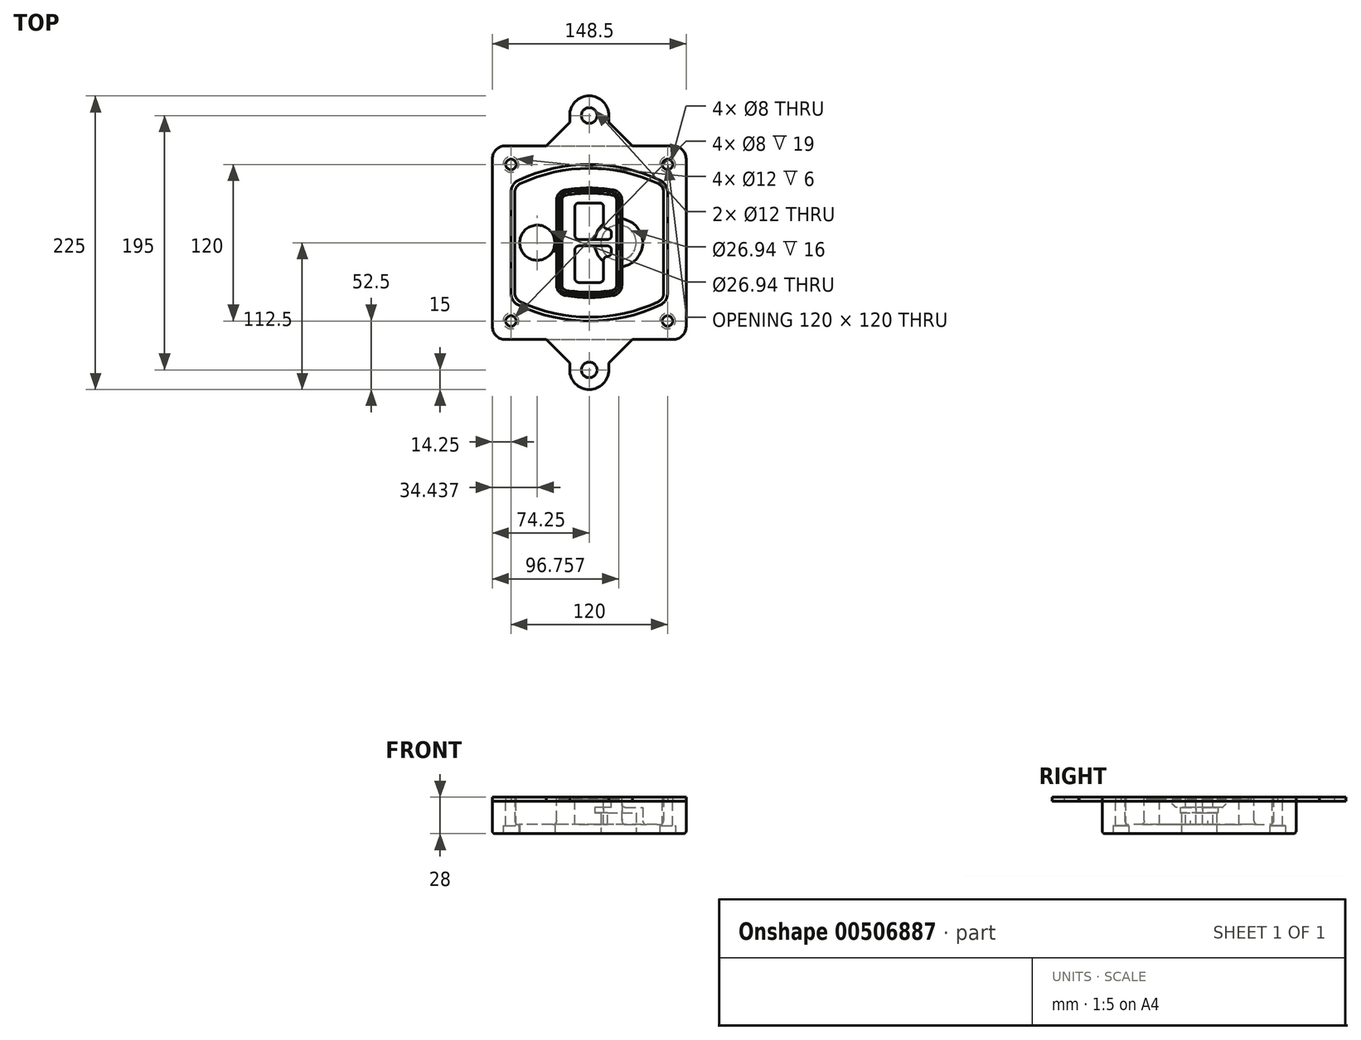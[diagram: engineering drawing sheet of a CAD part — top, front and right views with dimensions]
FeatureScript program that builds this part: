
annotation { "Feature Type Name" : "Feature", "Feature Type Description" : "" }
export const myFeature = defineFeature(function(context is Context, id is Id, definition is map)
    precondition{}
    {
        {
            var Q0;
            Q0=qCreatedBy(makeId("Top.planeOp"),FACE);
            var sketch = newSketch(context, id + "F0", { "sketchPlane" : qUnion([Q0])});
            skPoint(sketch, "E0.rect.middle", {"position": v(0, 0) * mm});
            skLineSegment(sketch, "E1.bottom", {"start": v(-64.25, -74.25) * mm, "end": v(64.25, -74.25) * mm});
            skLineSegment(sketch, "E1.top", {"start": v(-64.25, 74.25) * mm, "end": v(64.25, 74.25) * mm});
            skLineSegment(sketch, "E1.left", {"start": v(-74.25, -64.25) * mm, "end": v(-74.25, 64.25) * mm});
            skLineSegment(sketch, "E1.right", {"start": v(74.25, -64.25) * mm, "end": v(74.25, 64.25) * mm});
            skLineSegment(sketch, "E2", {"start": v(-74.25, 74.25) * mm, "end": v(74.25, -74.25) * mm, "construction": true});
            skLineSegment(sketch, "E3", {"start": v(74.25, 74.25) * mm, "end": v(-74.25, -74.25) * mm, "construction": true});
            skCircle(sketch, "E4", {"center": v(-60, 60) * mm, "radius": 4 * mm});
            skCircle(sketch, "E5", {"center": v(60, 60) * mm, "radius": 4 * mm});
            skCircle(sketch, "E6", {"center": v(60, -60) * mm, "radius": 4 * mm});
            skCircle(sketch, "E7", {"center": v(-60, -60) * mm, "radius": 4 * mm});
            skLineSegment(sketch, "E8", {"start": v(-60, 60) * mm, "end": v(60, 60) * mm, "construction": true});
            skLineSegment(sketch, "E9", {"start": v(60, 60) * mm, "end": v(60, -60) * mm, "construction": true});
            skLineSegment(sketch, "E10", {"start": v(60, -60) * mm, "end": v(-60, -60) * mm, "construction": true});
            skLineSegment(sketch, "E11", {"start": v(-60, -60) * mm, "end": v(-60, 60) * mm, "construction": true});
            skLineSegment(sketch, "E12", {"start": v(-60, 38.83) * mm, "end": v(-60, -38.83) * mm});
            skLineSegment(sketch, "E13", {"start": v(60, 38.83) * mm, "end": v(60, -38.83) * mm});
            skArc(sketch, "E14", {"start": v(54.26, 47.88) * mm, "mid": v(0, 60) * mm, "end": v(-54.26, 47.88) * mm});
            skArc(sketch, "E15", {"start": v(-54.26, -47.88) * mm, "mid": v(0, -60) * mm, "end": v(54.26, -47.88) * mm});
            skLineSegment(sketch, "E16", {"start": v(-60, 0) * mm, "end": v(60, 0) * mm, "construction": true});
            skPoint(sketch, "E17.visualSharp", {"position": v(-60, -45) * mm});
            skArc(sketch, "E17.filletArc", {"start": v(-60, -38.83) * mm, "mid": v(-58.44, -44.2) * mm, "end": v(-54.26, -47.88) * mm});
            skPoint(sketch, "E18.visualSharp", {"position": v(-60, 45) * mm});
            skArc(sketch, "E18.filletArc", {"start": v(-54.26, 47.88) * mm, "mid": v(-58.44, 44.2) * mm, "end": v(-60, 38.83) * mm});
            skPoint(sketch, "E19.visualSharp", {"position": v(60, 45) * mm});
            skArc(sketch, "E19.filletArc", {"start": v(60, 38.83) * mm, "mid": v(58.44, 44.2) * mm, "end": v(54.26, 47.88) * mm});
            skPoint(sketch, "E20.visualSharp", {"position": v(60, -45) * mm});
            skArc(sketch, "E20.filletArc", {"start": v(54.26, -47.88) * mm, "mid": v(58.44, -44.2) * mm, "end": v(60, -38.83) * mm});
            skPoint(sketch, "E21.visualSharp", {"position": v(-74.25, 74.25) * mm});
            skArc(sketch, "E21.filletArc", {"start": v(-64.25, 74.25) * mm, "mid": v(-71.32, 71.32) * mm, "end": v(-74.25, 64.25) * mm});
            skPoint(sketch, "E22.visualSharp", {"position": v(74.25, 74.25) * mm});
            skArc(sketch, "E22.filletArc", {"start": v(74.25, 64.25) * mm, "mid": v(71.32, 71.32) * mm, "end": v(64.25, 74.25) * mm});
            skPoint(sketch, "E23.visualSharp", {"position": v(74.25, -74.25) * mm});
            skArc(sketch, "E23.filletArc", {"start": v(64.25, -74.25) * mm, "mid": v(71.32, -71.32) * mm, "end": v(74.25, -64.25) * mm});
            skPoint(sketch, "E24.visualSharp", {"position": v(-74.25, -74.25) * mm});
            skArc(sketch, "E24.filletArc", {"start": v(-74.25, -64.25) * mm, "mid": v(-71.32, -71.32) * mm, "end": v(-64.25, -74.25) * mm});
            skArc(sketch, "E25.0", {"start": v(57, 38.83) * mm, "mid": v(55.9, 42.58) * mm, "end": v(52.98, 45.17) * mm});
            skLineSegment(sketch, "E25.1", {"start": v(57, 38.83) * mm, "end": v(57, -38.83) * mm});
            skArc(sketch, "E25.2", {"start": v(52.98, -45.17) * mm, "mid": v(55.9, -42.58) * mm, "end": v(57, -38.83) * mm});
            skArc(sketch, "E25.3", {"start": v(-52.98, -45.17) * mm, "mid": v(0, -57) * mm, "end": v(52.98, -45.17) * mm});
            skArc(sketch, "E25.4", {"start": v(-57, -38.83) * mm, "mid": v(-55.9, -42.58) * mm, "end": v(-52.98, -45.17) * mm});
            skArc(sketch, "E25.5", {"start": v(52.98, 45.17) * mm, "mid": v(0, 57) * mm, "end": v(-52.98, 45.17) * mm});
            skLineSegment(sketch, "E25.6", {"start": v(-57, 38.83) * mm, "end": v(-57, -38.83) * mm});
            skArc(sketch, "E25.7", {"start": v(-52.98, 45.17) * mm, "mid": v(-55.9, 42.58) * mm, "end": v(-57, 38.83) * mm});
            skArc(sketch, "E26.0", {"start": v(-55.96, 51.5) * mm, "mid": v(-61.82, 46.33) * mm, "end": v(-64, 38.83) * mm});
            skArc(sketch, "E26.1", {"start": v(55.96, 51.5) * mm, "mid": v(0, 64) * mm, "end": v(-55.96, 51.5) * mm});
            skArc(sketch, "E26.2", {"start": v(64, 38.83) * mm, "mid": v(61.82, 46.33) * mm, "end": v(55.96, 51.5) * mm});
            skLineSegment(sketch, "E26.3", {"start": v(64, 38.83) * mm, "end": v(64, -38.83) * mm});
            skArc(sketch, "E26.4", {"start": v(55.96, -51.5) * mm, "mid": v(61.82, -46.33) * mm, "end": v(64, -38.83) * mm});
            skLineSegment(sketch, "E26.5", {"start": v(-64, 38.83) * mm, "end": v(-64, -38.83) * mm});
            skArc(sketch, "E26.6", {"start": v(-55.96, -51.5) * mm, "mid": v(0, -64) * mm, "end": v(55.96, -51.5) * mm});
            skArc(sketch, "E26.7", {"start": v(-64, -38.83) * mm, "mid": v(-61.82, -46.33) * mm, "end": v(-55.96, -51.5) * mm});
            skSolve(sketch);
        }
        {
            var Q0;
            Q0=makeQuery(id+"F0.imprint","IMPRINT",FACE,{"disambiguationData":[TD([[makeQuery(id+"F0.imprint","IMPRINT",EDGE,{"derivedFrom":sQuery(id+"F0.wireOp",EDGE,"E1.bottom")}),1.0]])]});
            var Q1;
            Q1=makeQuery(id+"F0.imprint","IMPRINT",FACE,{"disambiguationData":[TD([[makeQuery(id+"F0.imprint","IMPRINT",EDGE,{"derivedFrom":sQuery(id+"F0.wireOp",EDGE,"E12")}),1.0]])]});
            var Q2;
            Q2=makeQuery(id+"F0.imprint","IMPRINT",FACE,{"disambiguationData":[TD([[makeQuery(id+"F0.imprint","IMPRINT",EDGE,{"derivedFrom":sQuery(id+"F0.wireOp",EDGE,"E25.0")}),1.0]])]});
            var Q3;
            Q3=makeQuery(id+"F0.imprint","IMPRINT",FACE,{"disambiguationData":[TD([[makeQuery(id+"F0.imprint","IMPRINT",EDGE,{"derivedFrom":sQuery(id+"F0.wireOp",EDGE,"E12")}),-1.0]])]});
            extrude(context, id + "F1", {"entities" : qUnion([Q0, Q1, Q2, Q3]), "oppositeDirection" : true, "depth" : 25 * mm, "offsetDistance" : 25 * mm});
        }
        {
            var Q0;
            Q0=makeQuery(id+"F0.imprint","IMPRINT",FACE,{"disambiguationData":[TD([[makeQuery(id+"F0.imprint","IMPRINT",EDGE,{"derivedFrom":sQuery(id+"F0.wireOp",EDGE,"E12")}),1.0]])]});
            extrude(context, id + "F2", {"entities" : qUnion([Q0]), "operationType" : NewBodyOperationType.ADD, "depth" : 3 * mm});
        }
        {
            var Q0;
            Q0=makeQuery(id+"F0.imprint","IMPRINT",FACE,{"disambiguationData":[TD([[makeQuery(id+"F0.imprint","IMPRINT",EDGE,{"derivedFrom":sQuery(id+"F0.wireOp",EDGE,"E25.0")}),1.0]])]});
            extrude(context, id + "F3", {"entities" : qUnion([Q0]), "operationType" : NewBodyOperationType.REMOVE, "oppositeDirection" : true, "depth" : 18 * mm});
        }
        {
            var Q0;
            Q0=makeQuery(id+"F2.opExtrude","CAP_FACE",FACE,{"disambiguationData":[OSD([sQuery(id+"F0.wireOp",EDGE,"E12"),sQuery(id+"F0.wireOp",EDGE,"E13"),sQuery(id+"F0.wireOp",EDGE,"E14"),sQuery(id+"F0.wireOp",EDGE,"E15"),sQuery(id+"F0.wireOp",EDGE,"E17.filletArc"),sQuery(id+"F0.wireOp",EDGE,"E18.filletArc"),sQuery(id+"F0.wireOp",EDGE,"E19.filletArc"),sQuery(id+"F0.wireOp",EDGE,"E20.filletArc"),sQuery(id+"F0.wireOp",EDGE,"E25.0"),sQuery(id+"F0.wireOp",EDGE,"E25.1"),sQuery(id+"F0.wireOp",EDGE,"E25.2"),sQuery(id+"F0.wireOp",EDGE,"E25.3"),sQuery(id+"F0.wireOp",EDGE,"E25.4"),sQuery(id+"F0.wireOp",EDGE,"E25.5"),sQuery(id+"F0.wireOp",EDGE,"E25.6"),sQuery(id+"F0.wireOp",EDGE,"E25.7")])],"isStart":false});
            var sketch = newSketch(context, id + "F4", { "sketchPlane" : qUnion([Q0])});
            skArc(sketch, "E27.0", {"start": v(-18.34, -40.45) * mm, "mid": v(0, -42) * mm, "end": v(18.34, -40.45) * mm});
            skArc(sketch, "E28.0", {"start": v(18.34, 40.45) * mm, "mid": v(0, 42) * mm, "end": v(-18.34, 40.45) * mm});
            skLineSegment(sketch, "E29", {"start": v(-25, 32.57) * mm, "end": v(-25, -32.57) * mm});
            skLineSegment(sketch, "E30", {"start": v(25, 32.57) * mm, "end": v(25, -32.57) * mm});
            skLineSegment(sketch, "E31", {"start": v(-25, 39.1) * mm, "end": v(25, 39.1) * mm, "construction": true});
            skLineSegment(sketch, "E32", {"start": v(-25, -39.1) * mm, "end": v(25, -39.1) * mm, "construction": true});
            skPoint(sketch, "E33.visualSharp", {"position": v(-25, 39.1) * mm});
            skArc(sketch, "E33.filletArc", {"start": v(-18.34, 40.45) * mm, "mid": v(-23.11, 37.73) * mm, "end": v(-25, 32.57) * mm});
            skPoint(sketch, "E34.visualSharp", {"position": v(25, 39.1) * mm});
            skArc(sketch, "E34.filletArc", {"start": v(25, 32.57) * mm, "mid": v(23.11, 37.73) * mm, "end": v(18.34, 40.45) * mm});
            skPoint(sketch, "E35.visualSharp", {"position": v(25, -39.1) * mm});
            skArc(sketch, "E35.filletArc", {"start": v(18.34, -40.45) * mm, "mid": v(23.11, -37.73) * mm, "end": v(25, -32.57) * mm});
            skPoint(sketch, "E36.visualSharp", {"position": v(-25, -39.1) * mm});
            skArc(sketch, "E36.filletArc", {"start": v(-25, -32.57) * mm, "mid": v(-23.11, -37.73) * mm, "end": v(-18.34, -40.45) * mm});
            skArc(sketch, "E37.0", {"start": v(52.98, 45.17) * mm, "mid": v(0, 57) * mm, "end": v(-52.98, 45.17) * mm});
            skArc(sketch, "E37.1", {"start": v(-52.98, 45.17) * mm, "mid": v(-55.9, 42.58) * mm, "end": v(-57, 38.83) * mm});
            skLineSegment(sketch, "E37.2", {"start": v(-57, 38.83) * mm, "end": v(-57, -38.83) * mm});
            skArc(sketch, "E37.3", {"start": v(-57, -38.83) * mm, "mid": v(-55.9, -42.58) * mm, "end": v(-52.98, -45.17) * mm});
            skArc(sketch, "E37.4", {"start": v(-52.98, -45.17) * mm, "mid": v(0, -57) * mm, "end": v(52.98, -45.17) * mm});
            skArc(sketch, "E37.5", {"start": v(52.98, -45.17) * mm, "mid": v(55.9, -42.58) * mm, "end": v(57, -38.83) * mm});
            skLineSegment(sketch, "E37.6", {"start": v(57, 38.83) * mm, "end": v(57, -38.83) * mm});
            skArc(sketch, "E37.7", {"start": v(57, 38.83) * mm, "mid": v(55.9, 42.58) * mm, "end": v(52.98, 45.17) * mm});
            skLineSegment(sketch, "E38.0", {"start": v(23, 32.57) * mm, "end": v(23, -32.57) * mm});
            skArc(sketch, "E38.1", {"start": v(18, -38.48) * mm, "mid": v(21.58, -36.44) * mm, "end": v(23, -32.57) * mm});
            skArc(sketch, "E38.2", {"start": v(-18, -38.48) * mm, "mid": v(0, -40) * mm, "end": v(18, -38.48) * mm});
            skArc(sketch, "E38.3", {"start": v(-23, -32.57) * mm, "mid": v(-21.58, -36.44) * mm, "end": v(-18, -38.48) * mm});
            skLineSegment(sketch, "E38.4", {"start": v(-23, 32.57) * mm, "end": v(-23, -32.57) * mm});
            skArc(sketch, "E38.5", {"start": v(23, 32.57) * mm, "mid": v(21.58, 36.44) * mm, "end": v(18, 38.48) * mm});
            skArc(sketch, "E38.6", {"start": v(-18, 38.48) * mm, "mid": v(-21.58, 36.44) * mm, "end": v(-23, 32.57) * mm});
            skArc(sketch, "E38.7", {"start": v(18, 38.48) * mm, "mid": v(0, 40) * mm, "end": v(-18, 38.48) * mm});
            skArc(sketch, "E39.0", {"start": v(21, 32.57) * mm, "mid": v(20.06, 35.15) * mm, "end": v(17.67, 36.5) * mm});
            skLineSegment(sketch, "E39.1", {"start": v(21, 32.57) * mm, "end": v(21, -32.57) * mm});
            skArc(sketch, "E39.2", {"start": v(17.67, -36.5) * mm, "mid": v(20.06, -35.15) * mm, "end": v(21, -32.57) * mm});
            skArc(sketch, "E39.3", {"start": v(-17.67, -36.5) * mm, "mid": v(0, -38) * mm, "end": v(17.67, -36.5) * mm});
            skArc(sketch, "E39.4", {"start": v(-21, -32.57) * mm, "mid": v(-20.06, -35.15) * mm, "end": v(-17.67, -36.5) * mm});
            skArc(sketch, "E39.5", {"start": v(17.67, 36.5) * mm, "mid": v(0, 38) * mm, "end": v(-17.67, 36.5) * mm});
            skLineSegment(sketch, "E39.6", {"start": v(-21, 32.57) * mm, "end": v(-21, -32.57) * mm});
            skArc(sketch, "E39.7", {"start": v(-17.67, 36.5) * mm, "mid": v(-20.06, 35.15) * mm, "end": v(-21, 32.57) * mm});
            skLineSegment(sketch, "E40", {"start": v(-25, 0) * mm, "end": v(25, 0) * mm, "construction": true});
            skLineSegment(sketch, "E41", {"start": v(-11, 5.5) * mm, "end": v(-11, 27.5) * mm});
            skLineSegment(sketch, "E42", {"start": v(-8, 30.5) * mm, "end": v(8, 30.5) * mm});
            skLineSegment(sketch, "E43", {"start": v(11, 27.5) * mm, "end": v(11, 13.5) * mm});
            skLineSegment(sketch, "E44", {"start": v(14, 10.5) * mm, "end": v(14, 10.5) * mm});
            skLineSegment(sketch, "E45", {"start": v(17, 7.5) * mm, "end": v(17, 5.5) * mm});
            skLineSegment(sketch, "E46", {"start": v(14, 2.5) * mm, "end": v(-8, 2.5) * mm});
            skPoint(sketch, "E47.visualSharp", {"position": v(-11, 30.5) * mm});
            skArc(sketch, "E47.filletArc", {"start": v(-8, 30.5) * mm, "mid": v(-10.12, 29.62) * mm, "end": v(-11, 27.5) * mm});
            skPoint(sketch, "E48.visualSharp", {"position": v(11, 30.5) * mm});
            skArc(sketch, "E48.filletArc", {"start": v(11, 27.5) * mm, "mid": v(10.12, 29.62) * mm, "end": v(8, 30.5) * mm});
            skPoint(sketch, "E49.visualSharp", {"position": v(11, 10.5) * mm});
            skArc(sketch, "E49.filletArc", {"start": v(11, 13.5) * mm, "mid": v(11.88, 11.38) * mm, "end": v(14, 10.5) * mm});
            skPoint(sketch, "E50.visualSharp", {"position": v(17, 10.5) * mm});
            skArc(sketch, "E50.filletArc", {"start": v(17, 7.5) * mm, "mid": v(16.12, 9.62) * mm, "end": v(14, 10.5) * mm});
            skPoint(sketch, "E51.visualSharp", {"position": v(17, 2.5) * mm});
            skArc(sketch, "E51.filletArc", {"start": v(14, 2.5) * mm, "mid": v(16.12, 3.38) * mm, "end": v(17, 5.5) * mm});
            skPoint(sketch, "E52.visualSharp", {"position": v(-11, 2.5) * mm});
            skArc(sketch, "E52.filletArc", {"start": v(-11, 5.5) * mm, "mid": v(-10.12, 3.38) * mm, "end": v(-8, 2.5) * mm});
            skLineSegment(sketch, "E53.0.MirrorCS", {"start": v(14, -2.5) * mm, "end": v(-8, -2.5) * mm});
            skArc(sketch, "E54.0.MirrorCS", {"start": v(-11, -5.5) * mm, "mid": v(-10.12, -3.38) * mm, "end": v(-8, -2.5) * mm});
            skLineSegment(sketch, "E55.0.MirrorCS", {"start": v(-11, -5.5) * mm, "end": v(-11, -27.5) * mm});
            skArc(sketch, "E56.0.MirrorCS", {"start": v(-8, -30.5) * mm, "mid": v(-10.12, -29.62) * mm, "end": v(-11, -27.5) * mm});
            skLineSegment(sketch, "E57.0.MirrorCS", {"start": v(-8, -30.5) * mm, "end": v(8, -30.5) * mm});
            skArc(sketch, "E58.0.MirrorCS", {"start": v(11, -27.5) * mm, "mid": v(10.12, -29.62) * mm, "end": v(8, -30.5) * mm});
            skLineSegment(sketch, "E59.0.MirrorCS", {"start": v(11, -27.5) * mm, "end": v(11, -13.5) * mm});
            skArc(sketch, "E60.0.MirrorCS", {"start": v(11, -13.5) * mm, "mid": v(11.88, -11.38) * mm, "end": v(14, -10.5) * mm});
            skArc(sketch, "E61.0.MirrorCS", {"start": v(17, -7.5) * mm, "mid": v(16.12, -9.62) * mm, "end": v(14, -10.5) * mm});
            skLineSegment(sketch, "E62.0.MirrorCS", {"start": v(17, -7.5) * mm, "end": v(17, -5.5) * mm});
            skArc(sketch, "E63.0.MirrorCS", {"start": v(14, -2.5) * mm, "mid": v(16.12, -3.38) * mm, "end": v(17, -5.5) * mm});
            skSolve(sketch);
        }
        {
            var Q0;
            Q0=makeQuery(id+"F4.imprint","IMPRINT",FACE,{"disambiguationData":[TD([[makeQuery(id+"F4.imprint","IMPRINT",EDGE,{"derivedFrom":sQuery(id+"F4.wireOp",EDGE,"E27.0")}),1.0]])]});
            var Q1;
            Q1=makeQuery(id+"F4.imprint","IMPRINT",FACE,{"disambiguationData":[TD([[makeQuery(id+"F4.imprint","IMPRINT",EDGE,{"derivedFrom":sQuery(id+"F4.wireOp",EDGE,"E38.0")}),-1.0]])]});
            var Q2;
            Q2=makeQuery(id+"F4.imprint","IMPRINT",FACE,{"disambiguationData":[TD([[makeQuery(id+"F4.imprint","IMPRINT",EDGE,{"derivedFrom":sQuery(id+"F4.wireOp",EDGE,"E39.0")}),1.0]])]});
            extrude(context, id + "F5", {"entities" : qUnion([Q0, Q1, Q2]), "operationType" : NewBodyOperationType.ADD, "endBound" : BoundingType.UP_TO_NEXT, "oppositeDirection" : true, "depth" : 25 * mm});
        }
        {
            var Q0;
            Q0=makeQuery(id+"F4.imprint","IMPRINT",FACE,{"disambiguationData":[TD([[makeQuery(id+"F4.imprint","IMPRINT",EDGE,{"derivedFrom":sQuery(id+"F4.wireOp",EDGE,"E38.0")}),-1.0]])]});
            extrude(context, id + "F6", {"entities" : qUnion([Q0]), "operationType" : NewBodyOperationType.REMOVE, "oppositeDirection" : true, "depth" : 2 * mm});
        }
        {
            var Q0;
            Q0=makeQuery(id+"F1.opExtrude","CAP_FACE",FACE,{"disambiguationData":[OSD([sQuery(id+"F0.wireOp",EDGE,"E1.bottom"),sQuery(id+"F0.wireOp",EDGE,"E1.top"),sQuery(id+"F0.wireOp",EDGE,"E1.left"),sQuery(id+"F0.wireOp",EDGE,"E1.right"),sQuery(id+"F0.wireOp",EDGE,"E4"),sQuery(id+"F0.wireOp",EDGE,"E5"),sQuery(id+"F0.wireOp",EDGE,"E6"),sQuery(id+"F0.wireOp",EDGE,"E7"),sQuery(id+"F0.wireOp",EDGE,"E21.filletArc"),sQuery(id+"F0.wireOp",EDGE,"E22.filletArc"),sQuery(id+"F0.wireOp",EDGE,"E23.filletArc"),sQuery(id+"F0.wireOp",EDGE,"E24.filletArc")])],"isStart":false});
            var sketch = newSketch(context, id + "F7", { "sketchPlane" : qUnion([Q0])});
            skCircle(sketch, "E64", {"center": v(22.5, 0) * mm, "radius": 13.47 * mm});
            skCircle(sketch, "E65", {"center": v(-39.81, 0) * mm, "radius": 13.47 * mm});
            skLineSegment(sketch, "E66", {"start": v(74.25, 0) * mm, "end": v(-74.25, 0) * mm});
            skCircle(sketch, "E67", {"center": v(22.5, 0) * mm, "radius": 18.47 * mm});
            skCircle(sketch, "E68", {"center": v(60, -60) * mm, "radius": 6 * mm});
            skCircle(sketch, "E69", {"center": v(-60, -60) * mm, "radius": 6 * mm});
            skCircle(sketch, "E70", {"center": v(-60, 60) * mm, "radius": 6 * mm});
            skCircle(sketch, "E71", {"center": v(60, 60) * mm, "radius": 6 * mm});
            skSolve(sketch);
        }
        {
            var Q0;
            {var subQ1=sQuery(id+"F7.wireOp",EDGE,"E66");var subQ4=sQuery(id+"F7.wireOp",EDGE,"E64");var subQ6=makeQuery(id+"F7.imprint","INTERSECT",VERTEX,{"disambiguationData":[OD(0.0)],"derivedFrom":[subQ4,subQ1]});Q0=makeQuery(id+"F7.imprint","IMPRINT",FACE,{"disambiguationData":[TD([[makeQuery(id+"F7.imprint","IMPRINT",EDGE,{"disambiguationData":[TD([[subQ6,-1.0]])],"derivedFrom":subQ4}),-1.0]])]});}
            var Q1;
            {var subQ0=sQuery(id+"F7.wireOp",EDGE,"E66");var subQ1=sQuery(id+"F7.wireOp",EDGE,"E64");var subQ3=makeQuery(id+"F7.imprint","INTERSECT",VERTEX,{"disambiguationData":[OD(0.0)],"derivedFrom":[subQ1,subQ0]});Q1=makeQuery(id+"F7.imprint","IMPRINT",FACE,{"disambiguationData":[TD([[makeQuery(id+"F7.imprint","IMPRINT",EDGE,{"disambiguationData":[TD([[subQ3,-1.0]])],"derivedFrom":subQ1}),1.0]])]});}
            var Q2;
            {var subQ0=sQuery(id+"F7.wireOp",EDGE,"E66");var subQ1=sQuery(id+"F7.wireOp",EDGE,"E64");var subQ3=makeQuery(id+"F7.imprint","INTERSECT",VERTEX,{"disambiguationData":[OD(0.0)],"derivedFrom":[subQ1,subQ0]});Q2=makeQuery(id+"F7.imprint","IMPRINT",FACE,{"disambiguationData":[TD([[makeQuery(id+"F7.imprint","IMPRINT",EDGE,{"disambiguationData":[TD([[subQ3,1.0]])],"derivedFrom":subQ1}),1.0]])]});}
            var Q3;
            {var subQ1=sQuery(id+"F7.wireOp",EDGE,"E66");var subQ4=sQuery(id+"F7.wireOp",EDGE,"E64");var subQ6=makeQuery(id+"F7.imprint","INTERSECT",VERTEX,{"disambiguationData":[OD(0.0)],"derivedFrom":[subQ4,subQ1]});Q3=makeQuery(id+"F7.imprint","IMPRINT",FACE,{"disambiguationData":[TD([[makeQuery(id+"F7.imprint","IMPRINT",EDGE,{"disambiguationData":[TD([[subQ6,1.0]])],"derivedFrom":subQ4}),-1.0]])]});}
            extrude(context, id + "F8", {"entities" : qUnion([Q0, Q1, Q2, Q3]), "operationType" : NewBodyOperationType.ADD, "oppositeDirection" : true, "depth" : 20 * mm});
        }
        {
            var Q0;
            {var subQ0=sQuery(id+"F7.wireOp",EDGE,"E66");var subQ1=sQuery(id+"F7.wireOp",EDGE,"E64");var subQ3=makeQuery(id+"F7.imprint","INTERSECT",VERTEX,{"disambiguationData":[OD(0.0)],"derivedFrom":[subQ1,subQ0]});Q0=makeQuery(id+"F7.imprint","IMPRINT",FACE,{"disambiguationData":[TD([[makeQuery(id+"F7.imprint","IMPRINT",EDGE,{"disambiguationData":[TD([[subQ3,-1.0]])],"derivedFrom":subQ1}),1.0]])]});}
            var Q1;
            {var subQ0=sQuery(id+"F7.wireOp",EDGE,"E66");var subQ1=sQuery(id+"F7.wireOp",EDGE,"E64");var subQ3=makeQuery(id+"F7.imprint","INTERSECT",VERTEX,{"disambiguationData":[OD(0.0)],"derivedFrom":[subQ1,subQ0]});Q1=makeQuery(id+"F7.imprint","IMPRINT",FACE,{"disambiguationData":[TD([[makeQuery(id+"F7.imprint","IMPRINT",EDGE,{"disambiguationData":[TD([[subQ3,1.0]])],"derivedFrom":subQ1}),1.0]])]});}
            extrude(context, id + "F9", {"entities" : qUnion([Q0, Q1]), "operationType" : NewBodyOperationType.REMOVE, "oppositeDirection" : true, "depth" : 16 * mm});
        }
        {
            var Q0;
            {var subQ0=sQuery(id+"F7.wireOp",EDGE,"E66");var subQ1=sQuery(id+"F7.wireOp",EDGE,"E65");var subQ3=makeQuery(id+"F7.imprint","INTERSECT",VERTEX,{"disambiguationData":[OD(0.0)],"derivedFrom":[subQ1,subQ0]});Q0=makeQuery(id+"F7.imprint","IMPRINT",FACE,{"disambiguationData":[TD([[makeQuery(id+"F7.imprint","IMPRINT",EDGE,{"disambiguationData":[TD([[subQ3,-1.0]])],"derivedFrom":subQ1}),1.0]])]});}
            var Q1;
            {var subQ0=sQuery(id+"F7.wireOp",EDGE,"E66");var subQ1=sQuery(id+"F7.wireOp",EDGE,"E65");var subQ3=makeQuery(id+"F7.imprint","INTERSECT",VERTEX,{"disambiguationData":[OD(0.0)],"derivedFrom":[subQ1,subQ0]});Q1=makeQuery(id+"F7.imprint","IMPRINT",FACE,{"disambiguationData":[TD([[makeQuery(id+"F7.imprint","IMPRINT",EDGE,{"disambiguationData":[TD([[subQ3,1.0]])],"derivedFrom":subQ1}),1.0]])]});}
            extrude(context, id + "F10", {"entities" : qUnion([Q0, Q1]), "operationType" : NewBodyOperationType.REMOVE, "oppositeDirection" : true, "depth" : 25 * mm, "offsetDistance" : 25 * mm});
        }
        {
            var Q0;
            Q0=makeQuery(id+"F7.imprint","IMPRINT",FACE,{"disambiguationData":[TD([[makeQuery(id+"F7.imprint","IMPRINT",EDGE,{"derivedFrom":sQuery(id+"F7.wireOp",EDGE,"E68")}),1.0]])]});
            var Q1;
            Q1=makeQuery(id+"F7.imprint","IMPRINT",FACE,{"disambiguationData":[TD([[makeQuery(id+"F7.imprint","IMPRINT",EDGE,{"derivedFrom":makeQuery(id+"F1.opExtrude","CAP_EDGE",EDGE,{"disambiguationData":[OSD([sQuery(id+"F0.wireOp",EDGE,"E5")])],"isStart":false})}),-1.0]])]});
            var Q2;
            Q2=makeQuery(id+"F7.imprint","IMPRINT",FACE,{"disambiguationData":[TD([[makeQuery(id+"F7.imprint","IMPRINT",EDGE,{"derivedFrom":sQuery(id+"F7.wireOp",EDGE,"E69")}),1.0]])]});
            var Q3;
            Q3=makeQuery(id+"F7.imprint","IMPRINT",FACE,{"disambiguationData":[TD([[makeQuery(id+"F7.imprint","IMPRINT",EDGE,{"derivedFrom":makeQuery(id+"F1.opExtrude","CAP_EDGE",EDGE,{"disambiguationData":[OSD([sQuery(id+"F0.wireOp",EDGE,"E4")])],"isStart":false})}),-1.0]])]});
            var Q4;
            Q4=makeQuery(id+"F7.imprint","IMPRINT",FACE,{"disambiguationData":[TD([[makeQuery(id+"F7.imprint","IMPRINT",EDGE,{"derivedFrom":sQuery(id+"F7.wireOp",EDGE,"E70")}),1.0]])]});
            var Q5;
            Q5=makeQuery(id+"F7.imprint","IMPRINT",FACE,{"disambiguationData":[TD([[makeQuery(id+"F7.imprint","IMPRINT",EDGE,{"derivedFrom":makeQuery(id+"F1.opExtrude","CAP_EDGE",EDGE,{"disambiguationData":[OSD([sQuery(id+"F0.wireOp",EDGE,"E7")])],"isStart":false})}),-1.0]])]});
            var Q6;
            Q6=makeQuery(id+"F7.imprint","IMPRINT",FACE,{"disambiguationData":[TD([[makeQuery(id+"F7.imprint","IMPRINT",EDGE,{"derivedFrom":sQuery(id+"F7.wireOp",EDGE,"E71")}),1.0]])]});
            var Q7;
            Q7=makeQuery(id+"F7.imprint","IMPRINT",FACE,{"disambiguationData":[TD([[makeQuery(id+"F7.imprint","IMPRINT",EDGE,{"derivedFrom":makeQuery(id+"F1.opExtrude","CAP_EDGE",EDGE,{"disambiguationData":[OSD([sQuery(id+"F0.wireOp",EDGE,"E6")])],"isStart":false})}),-1.0]])]});
            extrude(context, id + "F11", {"entities" : qUnion([Q0, Q1, Q2, Q3, Q4, Q5, Q6, Q7]), "operationType" : NewBodyOperationType.REMOVE, "oppositeDirection" : true, "depth" : 6 * mm, "offsetDistance" : 25 * mm});
        }
        {
            var Q0;
            Q0=makeQuery(id+"F9.boolean.opBoolean","COPY",FACE,{"derivedFrom":makeQuery(id+"F9.opExtrude","CAP_FACE",FACE,{"disambiguationData":[OSD([sQuery(id+"F7.wireOp",EDGE,"E64")])],"isStart":false})});
            var sketch = newSketch(context, id + "F12", { "sketchPlane" : qUnion([Q0])});
            skArc(sketch, "E72.0", {"start": v(11, 14.45) * mm, "mid": v(6.45, 9.13) * mm, "end": v(4.2, 2.5) * mm});
            skArc(sketch, "E72.1", {"start": v(4.2, -2.5) * mm, "mid": v(6.45, -9.13) * mm, "end": v(11, -14.45) * mm});
            skLineSegment(sketch, "E73", {"start": v(4.2, -2.5) * mm, "end": v(14, -2.5) * mm});
            skLineSegment(sketch, "E74.0", {"start": v(14, 2.5) * mm, "end": v(4.2, 2.5) * mm});
            skArc(sketch, "E74.1", {"start": v(14, 2.5) * mm, "mid": v(16.12, 3.38) * mm, "end": v(17, 5.5) * mm});
            skLineSegment(sketch, "E74.2", {"start": v(17, 7.5) * mm, "end": v(17, 5.5) * mm});
            skArc(sketch, "E74.3", {"start": v(17, 7.5) * mm, "mid": v(16.12, 9.62) * mm, "end": v(14, 10.5) * mm});
            skArc(sketch, "E74.4", {"start": v(11, 13.5) * mm, "mid": v(11.88, 11.38) * mm, "end": v(14, 10.5) * mm});
            skLineSegment(sketch, "E74.5", {"start": v(11, 14.45) * mm, "end": v(11, 13.5) * mm});
            skLineSegment(sketch, "E74.7", {"start": v(14, -2.5) * mm, "end": v(4.2, -2.5) * mm});
            skArc(sketch, "E74.8", {"start": v(14, -2.5) * mm, "mid": v(16.12, -3.38) * mm, "end": v(17, -5.5) * mm});
            skLineSegment(sketch, "E74.9", {"start": v(17, -7.5) * mm, "end": v(17, -5.5) * mm});
            skArc(sketch, "E74.10", {"start": v(17, -7.5) * mm, "mid": v(16.12, -9.62) * mm, "end": v(14, -10.5) * mm});
            skArc(sketch, "E74.11", {"start": v(11, -13.5) * mm, "mid": v(11.88, -11.38) * mm, "end": v(14, -10.5) * mm});
            skLineSegment(sketch, "E74.12", {"start": v(11, -14.45) * mm, "end": v(11, -13.5) * mm});
            skPoint(sketch, "E75.orphan", {"position": v(11, -27.5) * mm});
            skPoint(sketch, "E76.orphan", {"position": v(-8, -2.5) * mm});
            skPoint(sketch, "E77.orphan", {"position": v(-8, 2.5) * mm});
            skPoint(sketch, "E78.orphan", {"position": v(11, 27.5) * mm});
            skSolve(sketch);
        }
        {
            var Q0;
            {var subQ7=sQuery(id+"F12.wireOp",EDGE,"E72.0");var subQ14=sQuery(id+"F12.wireOp",EDGE,"E72.1");var subQ16=sQuery(id+"F12.wireOp",EDGE,"E74.1");var subQ18=sQuery(id+"F12.wireOp",EDGE,"E74.8");Q0=qUnion([makeQuery(id+"F12.imprint","IMPRINT",FACE,{"disambiguationData":[TD([[makeQuery(id+"F12.imprint","IMPRINT",EDGE,{"derivedFrom":subQ7}),1.0]])]}),makeQuery(id+"F12.imprint","IMPRINT",FACE,{"disambiguationData":[TD([[makeQuery(id+"F12.imprint","IMPRINT",EDGE,{"derivedFrom":subQ14}),1.0]])]}),makeQuery(id+"F12.imprint","IMPRINT",FACE,{"disambiguationData":[TD([[makeQuery(id+"F12.imprint","IMPRINT",EDGE,{"derivedFrom":subQ16}),1.0]])]}),makeQuery(id+"F12.imprint","IMPRINT",FACE,{"disambiguationData":[TD([[makeQuery(id+"F12.imprint","IMPRINT",EDGE,{"derivedFrom":subQ18}),-1.0]])]})]);}
            var Q1;
            Q1=makeQuery(id+"F5.boolean.opBoolean","SPLIT",FACE,{"disambiguationData":[TD([makeQuery(id+"F5.opExtrude","SWEPT_FACE",FACE,{"disambiguationData":[OSD([sQuery(id+"F4.wireOp",EDGE,"E41")])]})])],"derivedFrom":makeQuery(id+"F3.boolean.opBoolean","COPY",FACE,{"derivedFrom":makeQuery(id+"F3.opExtrude","CAP_FACE",FACE,{"disambiguationData":[OSD([sQuery(id+"F0.wireOp",EDGE,"E25.0"),sQuery(id+"F0.wireOp",EDGE,"E25.1"),sQuery(id+"F0.wireOp",EDGE,"E25.2"),sQuery(id+"F0.wireOp",EDGE,"E25.3"),sQuery(id+"F0.wireOp",EDGE,"E25.4"),sQuery(id+"F0.wireOp",EDGE,"E25.5"),sQuery(id+"F0.wireOp",EDGE,"E25.6"),sQuery(id+"F0.wireOp",EDGE,"E25.7")])],"isStart":false})})});
            extrude(context, id + "F13", {"entities" : qUnion([Q0]), "operationType" : NewBodyOperationType.REMOVE, "endBound" : BoundingType.UP_TO_SURFACE, "endBoundEntityFace" : qUnion([Q1]), "depth" : 25 * mm});
        }
        {
            var Q0;
            Q0=makeQuery(id+"F3.boolean.opBoolean","COPY",EDGE,{"derivedFrom":makeQuery(id+"F3.opExtrude","CAP_EDGE",EDGE,{"disambiguationData":[OSD([sQuery(id+"F0.wireOp",EDGE,"E25.6")])],"isStart":false})});
            var Q1;
            Q1=makeQuery(id+"F8.boolean.opBoolean","INTERSECT",EDGE,{"derivedFrom":[makeQuery(id+"F5.opExtrude","SWEPT_FACE",FACE,{"disambiguationData":[OSD([sQuery(id+"F4.wireOp",EDGE,"E30")])]}),makeQuery(id+"F8.opExtrude","CAP_FACE",FACE,{"disambiguationData":[OSD([sQuery(id+"F7.wireOp",EDGE,"E67")])],"isStart":false})]});
            var Q2;
            Q2=makeQuery(id+"F8.boolean.opBoolean","INTERSECT",EDGE,{"disambiguationData":[OD(1.0)],"derivedFrom":[makeQuery(id+"F5.opExtrude","SWEPT_FACE",FACE,{"disambiguationData":[OSD([sQuery(id+"F4.wireOp",EDGE,"E30")])]}),makeQuery(id+"F8.opExtrude","SWEPT_FACE",FACE,{"disambiguationData":[OSD([sQuery(id+"F7.wireOp",EDGE,"E67")])]})]});
            var Q3;
            {var subQ0=sQuery(id+"F4.wireOp",EDGE,"E30");Q3=makeQuery(id+"F8.boolean.opBoolean","SPLIT",EDGE,{"disambiguationData":[TD([makeQuery(id+"F5.opExtrude","SWEPT_FACE",FACE,{"disambiguationData":[OSD([sQuery(id+"F4.wireOp",EDGE,"E35.filletArc")])]})])],"derivedFrom":makeQuery(id+"F5.opExtrude","CAP_EDGE",EDGE,{"disambiguationData":[OSD([subQ0])],"isStart":false})});}
            var Q4;
            {var subQ0=sQuery(id+"F0.wireOp",EDGE,"E25.7");var subQ1=sQuery(id+"F0.wireOp",EDGE,"E25.1");var subQ2=sQuery(id+"F0.wireOp",EDGE,"E25.6");var subQ3=sQuery(id+"F0.wireOp",EDGE,"E25.5");var subQ4=sQuery(id+"F0.wireOp",EDGE,"E25.4");var subQ5=sQuery(id+"F0.wireOp",EDGE,"E25.0");var subQ6=sQuery(id+"F0.wireOp",EDGE,"E25.2");var subQ7=sQuery(id+"F0.wireOp",EDGE,"E25.3");Q4=makeQuery(id+"F8.boolean.opBoolean","INTERSECT",EDGE,{"derivedFrom":[makeQuery(id+"F5.boolean.opBoolean","SPLIT",FACE,{"disambiguationData":[TD([makeQuery(id+"F2.opExtrude","SWEPT_FACE",FACE,{"disambiguationData":[OSD([subQ5])]})])],"derivedFrom":makeQuery(id+"F3.boolean.opBoolean","COPY",FACE,{"derivedFrom":makeQuery(id+"F3.opExtrude","CAP_FACE",FACE,{"disambiguationData":[OSD([subQ5,subQ1,subQ6,subQ7,subQ4,subQ3,subQ2,subQ0])],"isStart":false})})}),makeQuery(id+"F8.opExtrude","SWEPT_FACE",FACE,{"disambiguationData":[OSD([sQuery(id+"F7.wireOp",EDGE,"E67")])]})]});}
            var Q5;
            Q5=makeQuery(id+"F8.boolean.opBoolean","INTERSECT",EDGE,{"disambiguationData":[OD(0.0)],"derivedFrom":[makeQuery(id+"F5.opExtrude","SWEPT_FACE",FACE,{"disambiguationData":[OSD([sQuery(id+"F4.wireOp",EDGE,"E30")])]}),makeQuery(id+"F8.opExtrude","SWEPT_FACE",FACE,{"disambiguationData":[OSD([sQuery(id+"F7.wireOp",EDGE,"E67")])]})]});
            fillet(context, id + "F14", {"entities" : qUnion([Q0, Q1, Q2, Q3, Q4, Q5]), "radius" : 3 * mm, "tangentPropagation" : true, "allowEdgeOverflow" : false});
        }
        {
            var Q0;
            Q0=makeQuery(id+"F1.opExtrude","CAP_EDGE",EDGE,{"disambiguationData":[OSD([sQuery(id+"F0.wireOp",EDGE,"E1.bottom")])],"isStart":false});
            fillet(context, id + "F15", {"entities" : qUnion([Q0]), "radius" : 2 * mm, "tangentPropagation" : true, "allowEdgeOverflow" : false});
        }
        {
            var Q0;
            {var subQ0=sQuery(id+"F0.wireOp",EDGE,"E21.filletArc");var subQ1=sQuery(id+"F0.wireOp",EDGE,"E7");var subQ2=sQuery(id+"F0.wireOp",EDGE,"E6");var subQ3=sQuery(id+"F0.wireOp",EDGE,"E5");var subQ4=sQuery(id+"F0.wireOp",EDGE,"E4");var subQ5=sQuery(id+"F0.wireOp",EDGE,"E22.filletArc");var subQ6=sQuery(id+"F0.wireOp",EDGE,"E1.bottom");var subQ7=sQuery(id+"F0.wireOp",EDGE,"E1.right");var subQ8=sQuery(id+"F0.wireOp",EDGE,"E1.top");var subQ9=sQuery(id+"F0.wireOp",EDGE,"E1.left");var subQ10=sQuery(id+"F0.wireOp",EDGE,"E23.filletArc");var subQ11=sQuery(id+"F0.wireOp",EDGE,"E24.filletArc");Q0=makeQuery(id+"F2.boolean.opBoolean","SPLIT",FACE,{"disambiguationData":[TD([makeQuery(id+"F1.opExtrude","SWEPT_FACE",FACE,{"disambiguationData":[OSD([subQ6])]})])],"derivedFrom":makeQuery(id+"F1.opExtrude","CAP_FACE",FACE,{"disambiguationData":[OSD([subQ6,subQ8,subQ9,subQ7,subQ4,subQ3,subQ2,subQ1,subQ0,subQ5,subQ10,subQ11])],"isStart":true})});}
            var sketch = newSketch(context, id + "F16", { "sketchPlane" : qUnion([Q0])});
            skLineSegment(sketch, "E79.0", {"start": v(-74.25, -64.25) * mm, "end": v(-74.25, 64.25) * mm});
            skArc(sketch, "E79.1", {"start": v(-64.25, 74.25) * mm, "mid": v(-71.32, 71.32) * mm, "end": v(-74.25, 64.25) * mm});
            skLineSegment(sketch, "E79.2", {"start": v(-64.25, 74.25) * mm, "end": v(64.25, 74.25) * mm});
            skArc(sketch, "E79.3", {"start": v(74.25, 64.25) * mm, "mid": v(71.32, 71.32) * mm, "end": v(64.25, 74.25) * mm});
            skLineSegment(sketch, "E79.4", {"start": v(74.25, -64.25) * mm, "end": v(74.25, 64.25) * mm});
            skArc(sketch, "E79.5", {"start": v(64.25, -74.25) * mm, "mid": v(71.32, -71.32) * mm, "end": v(74.25, -64.25) * mm});
            skLineSegment(sketch, "E79.6", {"start": v(-64.25, -74.25) * mm, "end": v(64.25, -74.25) * mm});
            skArc(sketch, "E79.7", {"start": v(-74.25, -64.25) * mm, "mid": v(-71.32, -71.32) * mm, "end": v(-64.25, -74.25) * mm});
            skArc(sketch, "E79.8", {"start": v(-54.26, -47.88) * mm, "mid": v(0, -60) * mm, "end": v(54.26, -47.88) * mm});
            skLineSegment(sketch, "E79.9", {"start": v(60, 38.83) * mm, "end": v(60, -38.83) * mm});
            skArc(sketch, "E79.10", {"start": v(54.26, -47.88) * mm, "mid": v(58.44, -44.2) * mm, "end": v(60, -38.83) * mm});
            skArc(sketch, "E79.11", {"start": v(60, 38.83) * mm, "mid": v(58.44, 44.2) * mm, "end": v(54.26, 47.88) * mm});
            skArc(sketch, "E79.12", {"start": v(54.26, 47.88) * mm, "mid": v(0, 60) * mm, "end": v(-54.26, 47.88) * mm});
            skArc(sketch, "E79.13", {"start": v(-54.26, 47.88) * mm, "mid": v(-58.44, 44.2) * mm, "end": v(-60, 38.83) * mm});
            skLineSegment(sketch, "E79.14", {"start": v(-60, 38.83) * mm, "end": v(-60, -38.83) * mm});
            skArc(sketch, "E79.15", {"start": v(-60, -38.83) * mm, "mid": v(-58.44, -44.2) * mm, "end": v(-54.26, -47.88) * mm});
            skCircle(sketch, "E79.16", {"center": v(-60, -60) * mm, "radius": 4 * mm});
            skCircle(sketch, "E79.17", {"center": v(-60, 60) * mm, "radius": 4 * mm});
            skCircle(sketch, "E79.18", {"center": v(60, 60) * mm, "radius": 4 * mm});
            skCircle(sketch, "E79.19", {"center": v(60, -60) * mm, "radius": 4 * mm});
            skLineSegment(sketch, "E80", {"start": v(33, -74.25) * mm, "end": v(15, -92.25) * mm});
            skLineSegment(sketch, "E81", {"start": v(15, -92.25) * mm, "end": v(15, -97.5) * mm});
            skLineSegment(sketch, "E82", {"start": v(-33, -74.25) * mm, "end": v(-15, -92.25) * mm});
            skLineSegment(sketch, "E83", {"start": v(-15, -92.25) * mm, "end": v(-15, -97.5) * mm});
            skArc(sketch, "E84", {"start": v(-15, -97.5) * mm, "mid": v(0, -112.5) * mm, "end": v(15, -97.5) * mm});
            skCircle(sketch, "E85", {"center": v(0, -97.5) * mm, "radius": 6 * mm});
            skLineSegment(sketch, "E86", {"start": v(0, -74.25) * mm, "end": v(0, -97.5) * mm, "construction": true});
            skLineSegment(sketch, "E87", {"start": v(74.25, 0) * mm, "end": v(-79.52, 0) * mm, "construction": true});
            skPoint(sketch, "E87.endSnap0", {"position": v(-74.25, 0) * mm});
            skArc(sketch, "E88.MirrorCS", {"start": v(-15, 97.5) * mm, "mid": v(0, 112.5) * mm, "end": v(15, 97.5) * mm});
            skLineSegment(sketch, "E89.MirrorCS", {"start": v(33, 74.25) * mm, "end": v(15, 92.25) * mm});
            skLineSegment(sketch, "E90.MirrorCS", {"start": v(-33, 74.25) * mm, "end": v(-15, 92.25) * mm});
            skLineSegment(sketch, "E91.MirrorCS", {"start": v(0, 74.25) * mm, "end": v(0, 97.5) * mm, "construction": true});
            skLineSegment(sketch, "E92.MirrorCS", {"start": v(-15, 92.25) * mm, "end": v(-15, 97.5) * mm});
            skLineSegment(sketch, "E93.MirrorCS", {"start": v(15, 92.25) * mm, "end": v(15, 97.5) * mm});
            skCircle(sketch, "E94.MirrorC", {"center": v(0, 97.5) * mm, "radius": 6 * mm});
            skSolve(sketch);
        }
        {
            var Q0;
            Q0 = qSketchRegion(id + "F16", true);
            var Q1;
            Q1=makeQuery(id+"F2.opExtrude","CAP_FACE",FACE,{"disambiguationData":[OSD([sQuery(id+"F0.wireOp",EDGE,"E12"),sQuery(id+"F0.wireOp",EDGE,"E13"),sQuery(id+"F0.wireOp",EDGE,"E14"),sQuery(id+"F0.wireOp",EDGE,"E15"),sQuery(id+"F0.wireOp",EDGE,"E17.filletArc"),sQuery(id+"F0.wireOp",EDGE,"E18.filletArc"),sQuery(id+"F0.wireOp",EDGE,"E19.filletArc"),sQuery(id+"F0.wireOp",EDGE,"E20.filletArc"),sQuery(id+"F0.wireOp",EDGE,"E25.0"),sQuery(id+"F0.wireOp",EDGE,"E25.1"),sQuery(id+"F0.wireOp",EDGE,"E25.2"),sQuery(id+"F0.wireOp",EDGE,"E25.3"),sQuery(id+"F0.wireOp",EDGE,"E25.4"),sQuery(id+"F0.wireOp",EDGE,"E25.5"),sQuery(id+"F0.wireOp",EDGE,"E25.6"),sQuery(id+"F0.wireOp",EDGE,"E25.7")])],"isStart":false});
            extrude(context, id + "F17", {"entities" : qUnion([Q0]), "endBound" : BoundingType.UP_TO_SURFACE, "depth" : 25 * mm, "endBoundEntityFace" : qUnion([Q1]), "offsetDistance" : 25 * mm});
        }
    });
